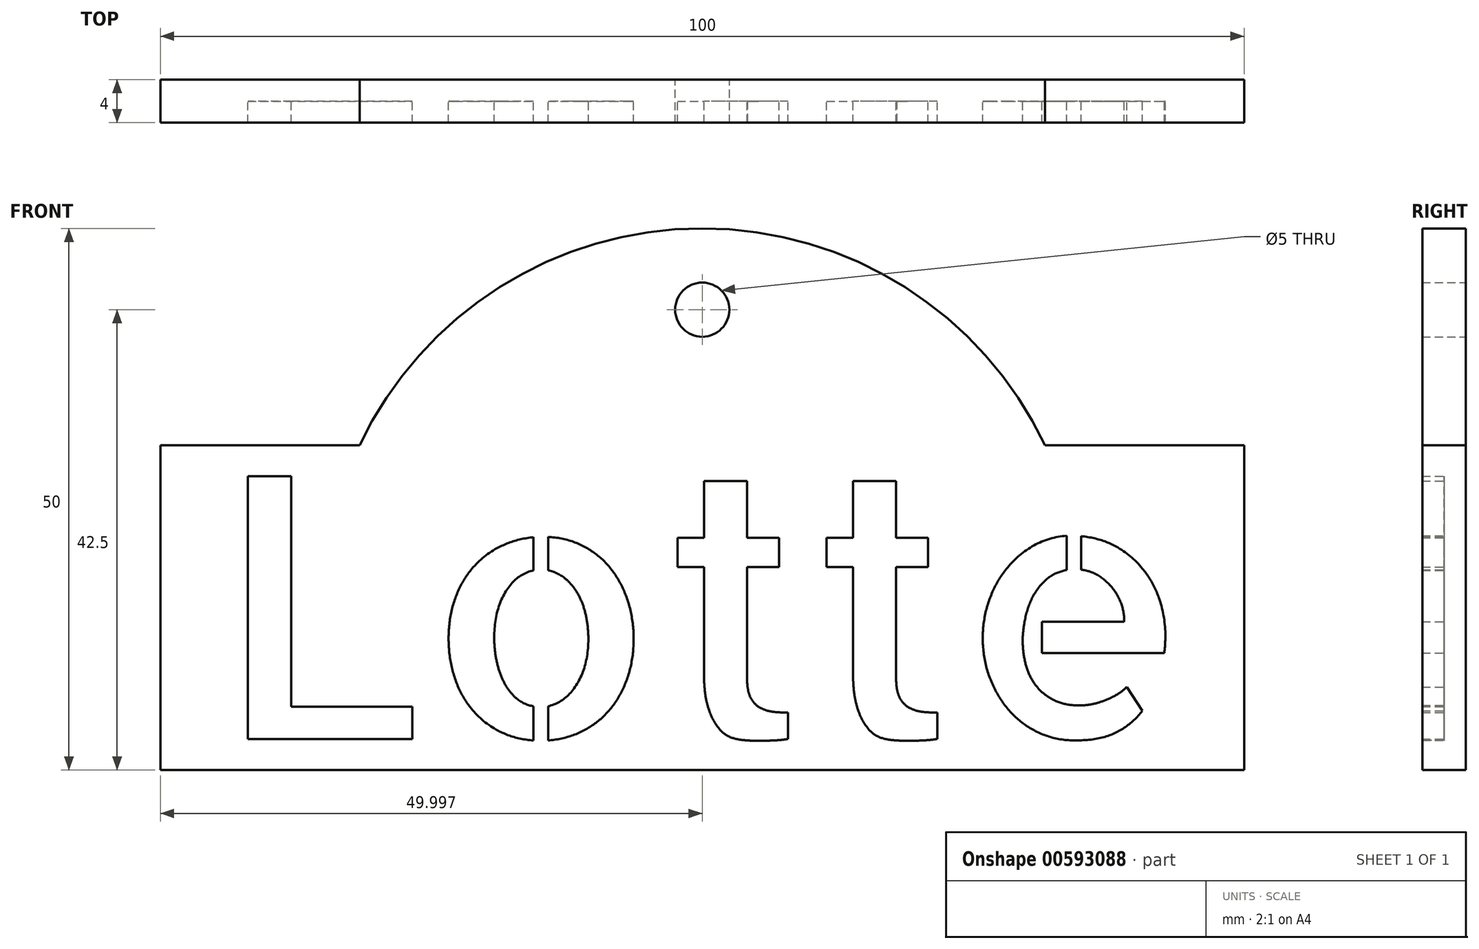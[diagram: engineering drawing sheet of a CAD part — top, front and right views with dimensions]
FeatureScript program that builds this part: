
annotation { "Feature Type Name" : "Feature", "Feature Type Description" : "" }
export const myFeature = defineFeature(function(context is Context, id is Id, definition is map)
    precondition{}
    {
        {
            var Q0;
            Q0=qCreatedBy(makeId("Front.planeOp"),FACE);
            var sketch = newSketch(context, id + "F0", { "sketchPlane" : qUnion([Q0])});
            skLineSegment(sketch, "E0.bottom", {"start": v(-68.08, 31.88) * mm, "end": v(-49.7, 31.88) * mm});
            skLineSegment(sketch, "E0.top", {"start": v(-68.08, 1.88) * mm, "end": v(31.92, 1.88) * mm});
            skLineSegment(sketch, "E0.left", {"start": v(-68.08, 31.88) * mm, "end": v(-68.08, 1.88) * mm});
            skLineSegment(sketch, "E0.right", {"start": v(31.92, 31.88) * mm, "end": v(31.92, 1.88) * mm});
            skArc(sketch, "E1", {"start": v(13.54, 31.88) * mm, "mid": v(-18.08, 51.88) * mm, "end": v(-49.7, 31.88) * mm});
            skCircle(sketch, "E2", {"center": v(-18.08, 44.38) * mm, "radius": 2.5 * mm});
            skText(sketch, "E3", { "text": "Lotte\n", "fontName": "AllertaStencil-Regular.ttf"});
            skPoint(sketch, "E4", {"position": v(-18.08, 4.75) * mm});
            skPoint(sketch, "E5.positionSnap0", {"position": v(-18.08, 1.88) * mm});
            skPoint(sketch, "E6", {"position": v(26.92, 16.88) * mm});
            skPoint(sketch, "E7", {"position": v(31.92, 16.88) * mm});
            skLineSegment(sketch, "E8.trimOffspring", {"start": v(13.54, 31.88) * mm, "end": v(31.92, 31.88) * mm});
            const initialGuessF0  = {"E3": [-0.06308, 0.00475, 1, 0, 0.02426]};
            skSetInitialGuess(sketch, initialGuessF0);
            skSolve(sketch);
        }
        {
            var Q0;
            Q0 = qSketchRegion(id + "F0", true);
            var Q1;
            Q1=makeQuery(id+"F0.imprint","IMPRINT",FACE,{"disambiguationData":[TD([[makeQuery(id+"F0.imprint","IMPRINT",EDGE,{"derivedFrom":sQuery(id+"F0.wireOp",EDGE,"E3.sketch_text.stroke-6")}),-1.0]])]});
            var Q2;
            Q2=makeQuery(id+"F0.imprint","IMPRINT",FACE,{"disambiguationData":[TD([[makeQuery(id+"F0.imprint","IMPRINT",EDGE,{"derivedFrom":sQuery(id+"F0.wireOp",EDGE,"E3.sketch_text.stroke-0")}),-1.0]])]});
            var Q3;
            Q3=makeQuery(id+"F0.imprint","IMPRINT",FACE,{"disambiguationData":[TD([[makeQuery(id+"F0.imprint","IMPRINT",EDGE,{"derivedFrom":sQuery(id+"F0.wireOp",EDGE,"E3.sketch_text.stroke-22")}),-1.0]])]});
            var Q4;
            Q4=makeQuery(id+"F0.imprint","IMPRINT",FACE,{"disambiguationData":[TD([[makeQuery(id+"F0.imprint","IMPRINT",EDGE,{"derivedFrom":sQuery(id+"F0.wireOp",EDGE,"E3.sketch_text.stroke-38")}),-1.0]])]});
            var Q5;
            Q5=makeQuery(id+"F0.imprint","IMPRINT",FACE,{"disambiguationData":[TD([[makeQuery(id+"F0.imprint","IMPRINT",EDGE,{"derivedFrom":sQuery(id+"F0.wireOp",EDGE,"E3.sketch_text.stroke-63")}),-1.0]])]});
            var Q6;
            Q6=makeQuery(id+"F0.imprint","IMPRINT",FACE,{"disambiguationData":[TD([[makeQuery(id+"F0.imprint","IMPRINT",EDGE,{"derivedFrom":sQuery(id+"F0.wireOp",EDGE,"E3.sketch_text.stroke-88")}),-1.0]])]});
            var Q7;
            Q7=makeQuery(id+"F0.imprint","IMPRINT",FACE,{"disambiguationData":[TD([[makeQuery(id+"F0.imprint","IMPRINT",EDGE,{"derivedFrom":sQuery(id+"F0.wireOp",EDGE,"E0.bottom")}),-1.0]])]});
            var Q8;
            Q8=makeQuery(id+"F0.imprint","IMPRINT",FACE,{"disambiguationData":[TD([[makeQuery(id+"F0.imprint","IMPRINT",EDGE,{"derivedFrom":sQuery(id+"F0.wireOp",EDGE,"E3.sketch_text.stroke-101")}),-1.0]])]});
            extrude(context, id + "F1", {"entities" : qUnion([Q0, Q1, Q2, Q3, Q4, Q5, Q6, Q7, Q8]), "depth" : 2 * mm, "offsetDistance" : 25 * mm});
        }
        {
            var Q0;
            Q0=makeQuery(id+"F0.imprint","IMPRINT",FACE,{"disambiguationData":[TD([[makeQuery(id+"F0.imprint","IMPRINT",EDGE,{"derivedFrom":sQuery(id+"F0.wireOp",EDGE,"E0.bottom")}),-1.0]])]});
            extrude(context, id + "F2", {"entities" : qUnion([Q0]), "operationType" : NewBodyOperationType.ADD, "depth" : 4 * mm, "offsetDistance" : 25 * mm});
        }
    });
